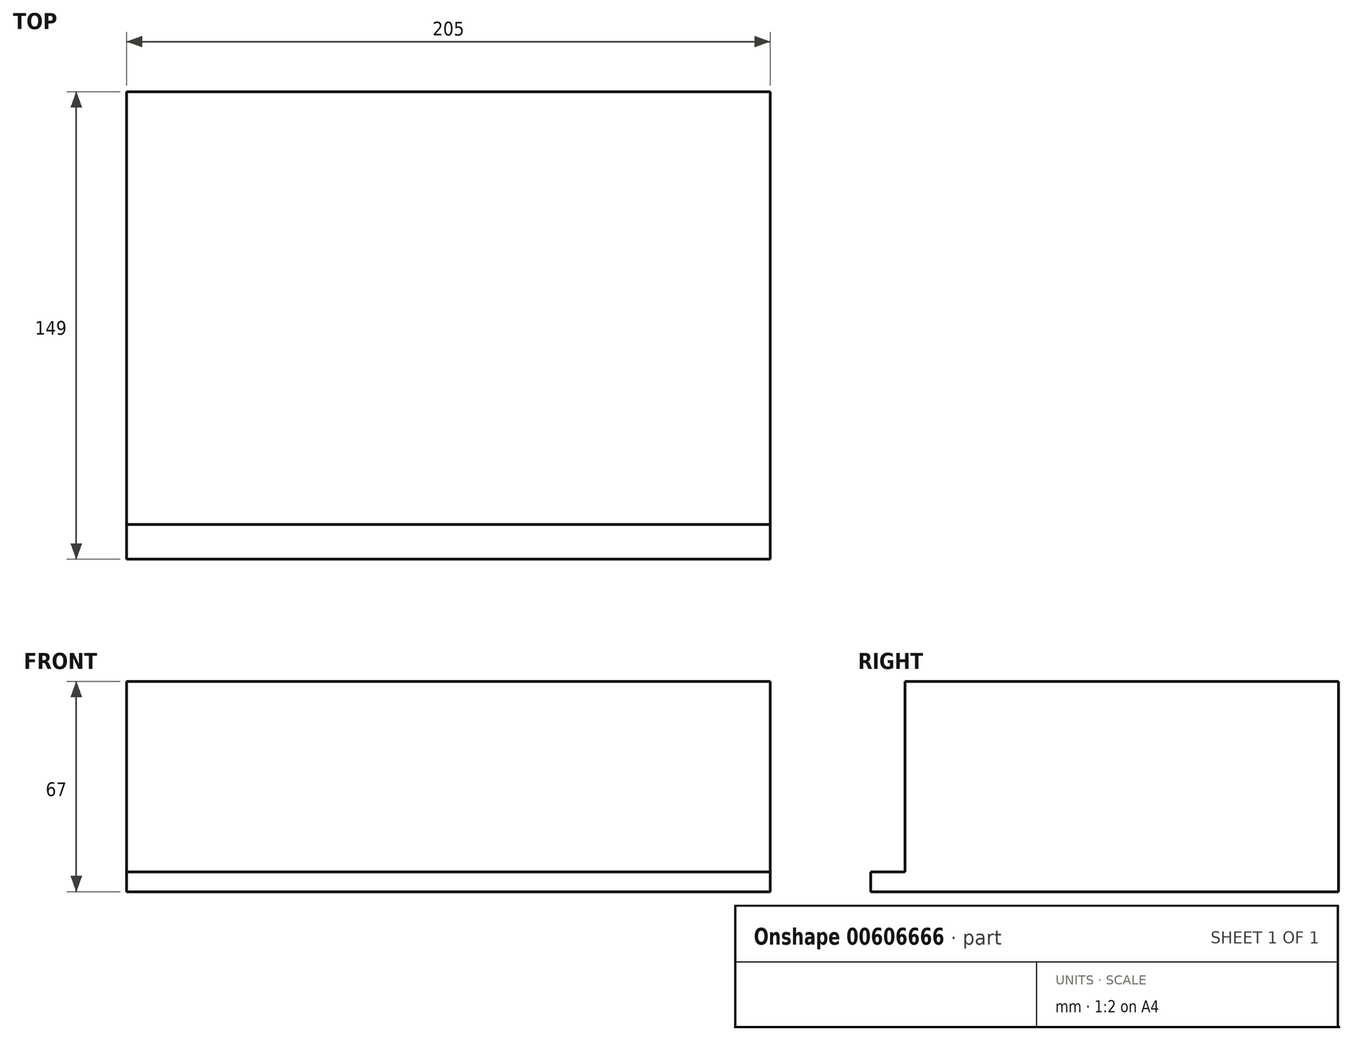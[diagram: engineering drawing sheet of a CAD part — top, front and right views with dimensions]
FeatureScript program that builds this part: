
annotation { "Feature Type Name" : "Feature", "Feature Type Description" : "" }
export const myFeature = defineFeature(function(context is Context, id is Id, definition is map)
    precondition{}
    {
        {
            var Q0;
            Q0=qCreatedBy(makeId("Top.planeOp"),FACE);
            var sketch = newSketch(context, id + "F0", { "sketchPlane" : qUnion([Q0])});
            skLineSegment(sketch, "E0.bottom", {"start": v(102.5, -69) * mm, "end": v(-102.5, -69) * mm});
            skLineSegment(sketch, "E0.top", {"start": v(102.5, 69) * mm, "end": v(-102.5, 69) * mm});
            skLineSegment(sketch, "E0.left", {"start": v(102.5, -69) * mm, "end": v(102.5, 69) * mm});
            skLineSegment(sketch, "E0.right", {"start": v(-102.5, -69) * mm, "end": v(-102.5, 69) * mm});
            skPoint(sketch, "E0.middle", {"position": v(0, 0) * mm});
            skSolve(sketch);
        }
        {
            var Q0;
            Q0 = qSketchRegion(id + "F0", true);
            extrude(context, id + "F1", {"entities" : qUnion([Q0]), "depth" : 67 * mm, "offsetDistance" : 25.4 * mm});
        }
        {
            var Q0;
            Q0=makeQuery(id+"F1.opExtrude","SWEPT_FACE",FACE,{"disambiguationData":[OSD([sQuery(id+"F0.wireOp",EDGE,"E0.bottom")])]});
            var sketch = newSketch(context, id + "F2", { "sketchPlane" : qUnion([Q0])});
            skLineSegment(sketch, "E1.bottom", {"start": v(-102.5, 0) * mm, "end": v(102.5, 0) * mm});
            skLineSegment(sketch, "E1.top", {"start": v(-102.5, 6.35) * mm, "end": v(102.5, 6.35) * mm});
            skLineSegment(sketch, "E1.left", {"start": v(-102.5, 0) * mm, "end": v(-102.5, 6.35) * mm});
            skLineSegment(sketch, "E1.right", {"start": v(102.5, 0) * mm, "end": v(102.5, 6.35) * mm});
            skSolve(sketch);
        }
        {
            var Q0;
            Q0 = qSketchRegion(id + "F2", true);
            extrude(context, id + "F3", {"entities" : qUnion([Q0]), "operationType" : NewBodyOperationType.ADD, "depth" : 11 * mm, "offsetDistance" : 25.4 * mm});
        }
    });
